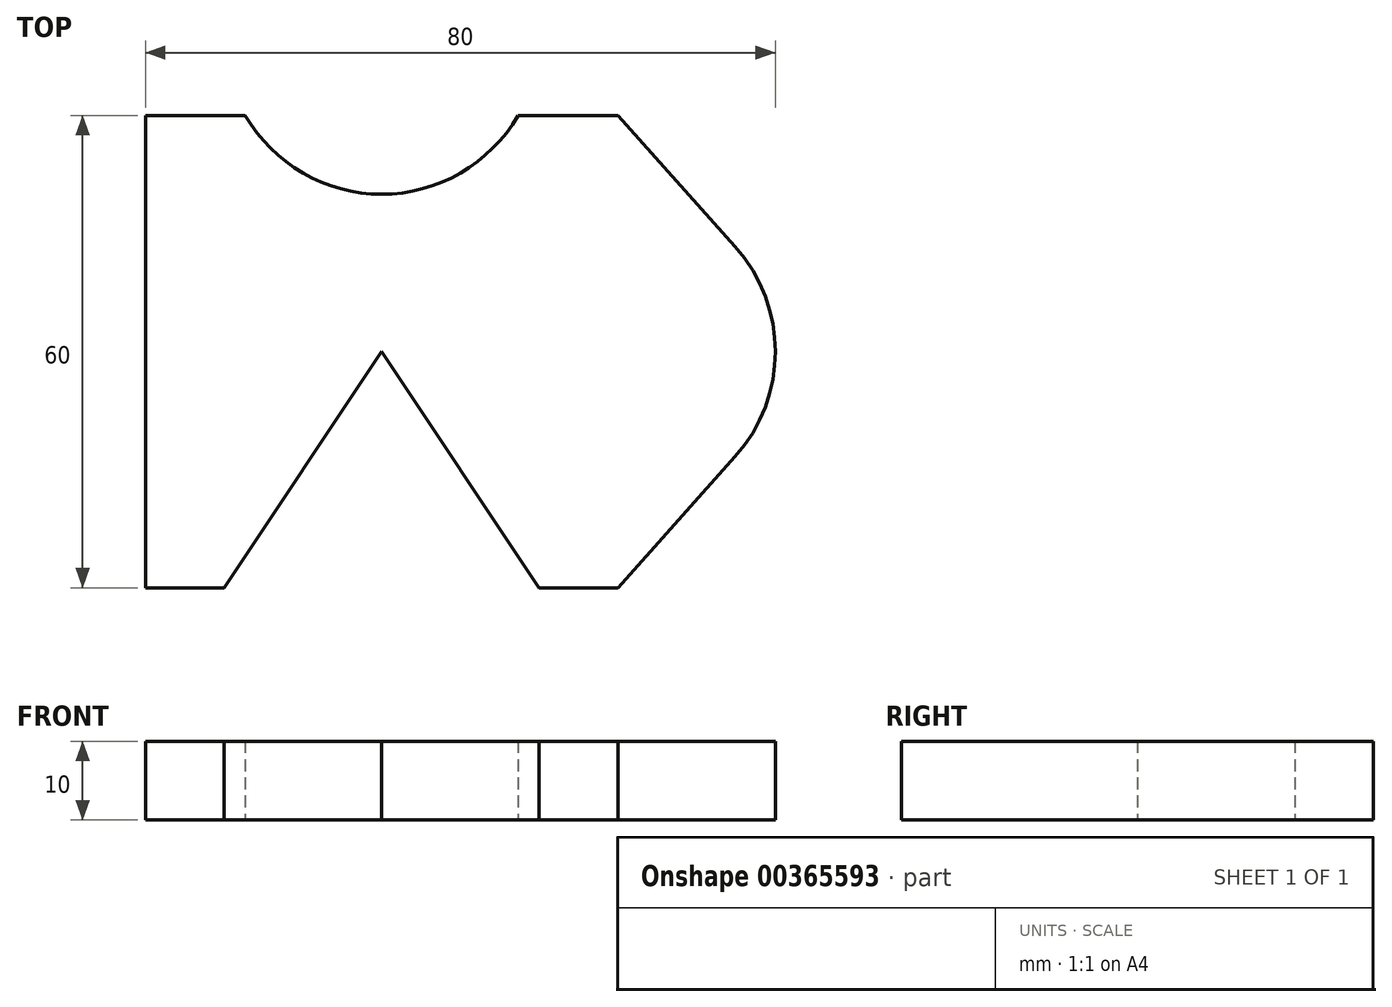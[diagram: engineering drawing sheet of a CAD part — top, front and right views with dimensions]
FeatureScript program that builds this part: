
annotation { "Feature Type Name" : "Feature", "Feature Type Description" : "" }
export const myFeature = defineFeature(function(context is Context, id is Id, definition is map)
    precondition{}
    {
        {
            var Q0;
            Q0=qCreatedBy(makeId("Top.planeOp"),FACE);
            var sketch = newSketch(context, id + "F0", { "sketchPlane" : qUnion([Q0])});
            skLineSegment(sketch, "E0", {"start": v(0, 0) * mm, "end": v(-20, -30) * mm});
            skLineSegment(sketch, "E1", {"start": v(-20, -30) * mm, "end": v(-30, -30) * mm});
            skLineSegment(sketch, "E2", {"start": v(-30, -30) * mm, "end": v(-30, 30) * mm});
            skLineSegment(sketch, "E3", {"start": v(-30, 30) * mm, "end": v(-17.32, 30) * mm});
            skArc(sketch, "E4", {"start": v(-17.32, 30) * mm, "mid": v(0, 20) * mm, "end": v(17.32, 30) * mm});
            skLineSegment(sketch, "E5", {"start": v(17.32, 30) * mm, "end": v(30, 30) * mm});
            skLineSegment(sketch, "E6", {"start": v(30, 30) * mm, "end": v(44.9, 13.33) * mm});
            skLineSegment(sketch, "E7", {"start": v(0, 0) * mm, "end": v(20, -30) * mm});
            skLineSegment(sketch, "E8", {"start": v(20, -30) * mm, "end": v(30, -30) * mm});
            skLineSegment(sketch, "E9", {"start": v(30, -30) * mm, "end": v(44.9, -13.33) * mm});
            skArc(sketch, "E10", {"start": v(44.9, -13.33) * mm, "mid": v(50, 0) * mm, "end": v(44.9, 13.33) * mm});
            skLineSegment(sketch, "E11", {"start": v(30, -30) * mm, "end": v(30, 30) * mm, "construction": true});
            skSolve(sketch);
        }
        {
            var Q0;
            Q0=makeQuery(id+"F0.imprint","IMPRINT",FACE,{"disambiguationData":[TD([[makeQuery(id+"F0.imprint","IMPRINT",EDGE,{"derivedFrom":sQuery(id+"F0.wireOp",EDGE,"E0")}),-1.0]])]});
            extrude(context, id + "F1", {"entities" : qUnion([Q0]), "depth" : 10 * mm});
        }
    });
